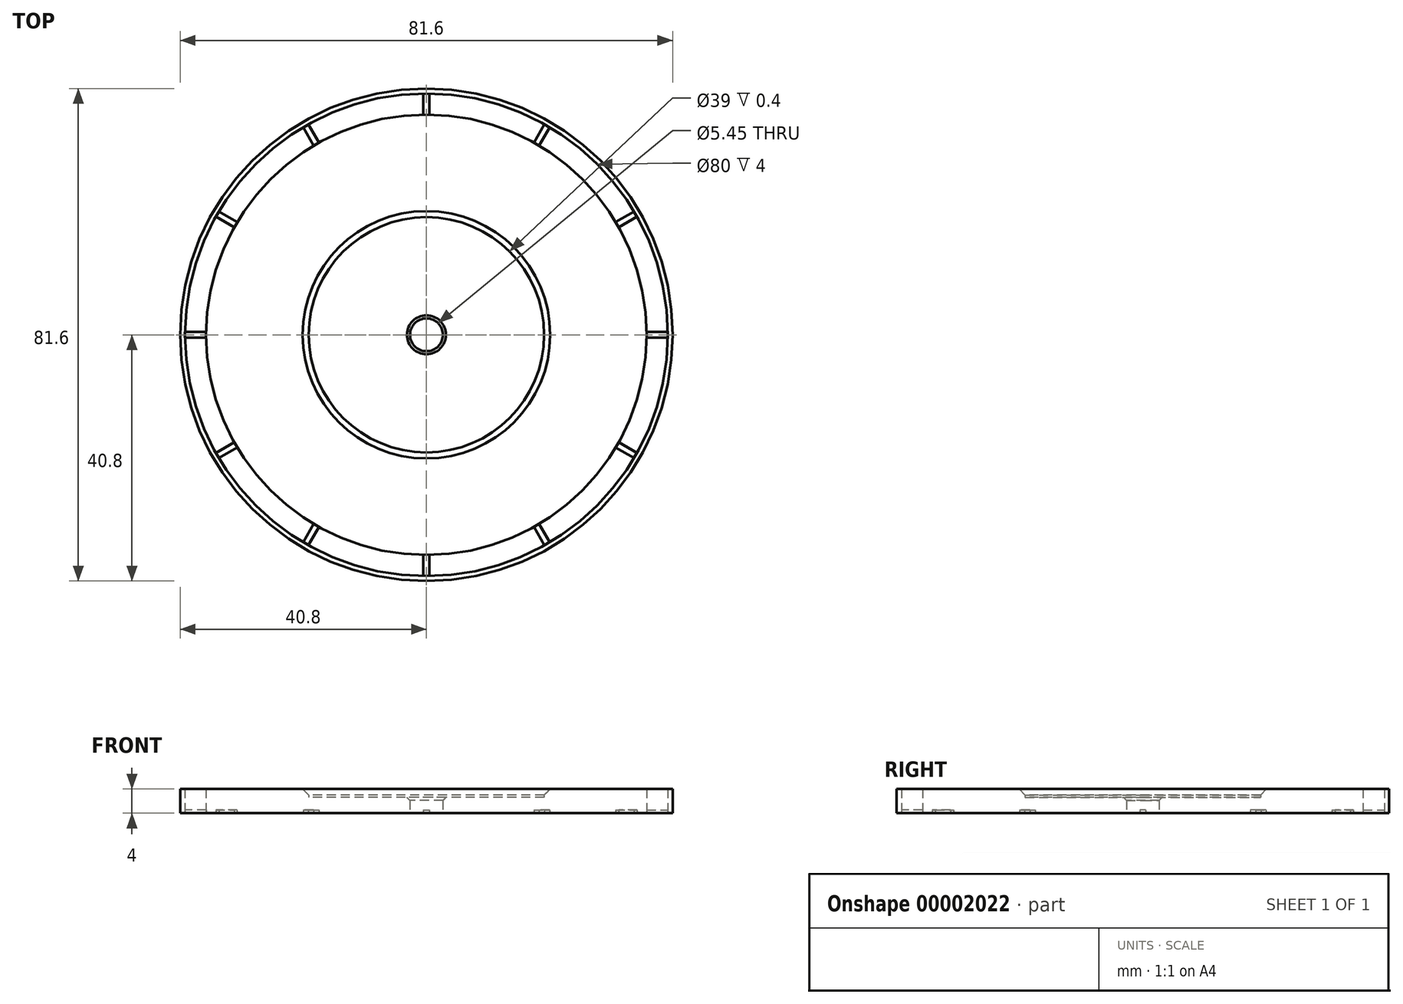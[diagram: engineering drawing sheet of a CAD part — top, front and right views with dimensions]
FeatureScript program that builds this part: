
annotation { "Feature Type Name" : "Feature", "Feature Type Description" : "" }
export const myFeature = defineFeature(function(context is Context, id is Id, definition is map)
    precondition{}
    {
        {
            var Q0;
            Q0=qCreatedBy(makeId("Top.planeOp"),FACE);
            var sketch = newSketch(context, id + "F0", { "sketchPlane" : qUnion([Q0])});
            skCircle(sketch, "E0", {"center": v(0, 0) * mm, "radius": 36.5 * mm});
            skCircle(sketch, "E1", {"center": v(0, 0) * mm, "radius": 40 * mm});
            skCircle(sketch, "E2", {"center": v(0, 0) * mm, "radius": 40.8 * mm});
            skCircle(sketch, "E3", {"center": v(0, 0) * mm, "radius": 19.5 * mm});
            skCircle(sketch, "E4", {"center": v(0, 0) * mm, "radius": 2.73 * mm});
            skSolve(sketch);
        }
        {
            var Q0;
            Q0=makeQuery(id+"F0.imprint","IMPRINT",FACE,{"disambiguationData":[TD([[makeQuery(id+"F0.imprint","IMPRINT",EDGE,{"derivedFrom":sQuery(id+"F0.wireOp",EDGE,"E0")}),1.0]])]});
            var Q1;
            Q1=makeQuery(id+"F0.imprint","IMPRINT",FACE,{"disambiguationData":[TD([[makeQuery(id+"F0.imprint","IMPRINT",EDGE,{"derivedFrom":sQuery(id+"F0.wireOp",EDGE,"E1")}),-1.0]])]});
            extrude(context, id + "F1", {"entities" : qUnion([Q0, Q1]), "depth" : 4 * mm});
        }
        {
            var Q0;
            Q0=makeQuery(id+"F0.imprint","IMPRINT",FACE,{"disambiguationData":[TD([[makeQuery(id+"F0.imprint","IMPRINT",EDGE,{"derivedFrom":sQuery(id+"F0.wireOp",EDGE,"E3")}),1.0]])]});
            extrude(context, id + "F2", {"entities" : qUnion([Q0]), "operationType" : NewBodyOperationType.ADD, "depth" : (8 - 5.4) * mm});
        }
        {
            var Q0;
            {var subQ0=sQuery(id+"F0.wireOp",EDGE,"E3");Q0=makeQuery(id+"F2.boolean.opBoolean","MERGE",FACE,{"derivedFrom":[makeQuery(id+"F1.opExtrude","CAP_FACE",FACE,{"disambiguationData":[OSD([sQuery(id+"F0.wireOp",EDGE,"E0"),subQ0])],"isStart":true}),makeQuery(id+"F2.opExtrude","CAP_FACE",FACE,{"disambiguationData":[OSD([subQ0,sQuery(id+"F0.wireOp",EDGE,"E4")])],"isStart":true})]});}
            var sketch = newSketch(context, id + "F3", { "sketchPlane" : qUnion([Q0])});
            skLineSegment(sketch, "E5", {"start": v(0, 0) * mm, "end": v(0, 38.64) * mm, "construction": true});
            skLineSegment(sketch, "E6", {"start": v(-0.5, 36.5) * mm, "end": v(-0.5, 40) * mm});
            skLineSegment(sketch, "E7", {"start": v(-0.5, 40) * mm, "end": v(0.5, 40) * mm});
            skLineSegment(sketch, "E8", {"start": v(0.5, 40) * mm, "end": v(0.5, 36.5) * mm});
            skPoint(sketch, "E9", {"position": v(0, 40) * mm});
            skCircle(sketch, "E10.0", {"center": v(0, 0) * mm, "radius": 40 * mm, "construction": true});
            skSolve(sketch);
        }
        {
            var Q0;
            {var subQ2=sQuery(id+"F3.wireOp",EDGE,"E6");Q0=makeQuery(id+"F3.imprint","IMPRINT",FACE,{"disambiguationData":[TD([[makeQuery(id+"F3.imprint","IMPRINT",EDGE,{"derivedFrom":subQ2}),-1.0]])]});}
            var Q1;
            Q1=makeQuery(id+"F1.opExtrude","CAP_FACE",FACE,{"disambiguationData":[OSD([sQuery(id+"F0.wireOp",EDGE,"E0"),sQuery(id+"F0.wireOp",EDGE,"E3")])],"isStart":false});
            extrude(context, id + "F4", {"entities" : qUnion([Q0]), "oppositeDirection" : true, "endBoundEntity" : qUnion([Q1]), "depth" : .5 * mm});
        }
        {
            var Q0;
            Q0=makeQuery(id+"F4.opExtrude","SWEPT_BODY",BODY,{"disambiguationData":[OSD([sQuery(id+"F0.wireOp",EDGE,"E0"),sQuery(id+"F3.wireOp",EDGE,"E6"),sQuery(id+"F3.wireOp",EDGE,"E7"),sQuery(id+"F3.wireOp",EDGE,"E8")])]});
            var Q1;
            Q1=makeQuery(id+"F1.opExtrude","SWEPT_FACE",FACE,{"disambiguationData":[OSD([sQuery(id+"F0.wireOp",EDGE,"E3")])]});
            circularPattern(context, id + "F5", {"entities" : qUnion([Q0]), "axis" : qUnion([Q1]), "angle" : 360 * degree, "instanceCount" : round(12), "equalSpace" : true});
        }
        {
            var Q0;
            Q0=makeQuery(id+"F1.opExtrude","CAP_EDGE",EDGE,{"disambiguationData":[OSD([sQuery(id+"F0.wireOp",EDGE,"E3")])],"isStart":false});
            chamfer(context, id + "F6", {"entities" : qUnion([Q0]), "width" : 1 * mm, "tangentPropagation" : true});
        }
        {
            var Q0;
            Q0=makeQuery(id+"F2.opExtrude","CAP_EDGE",EDGE,{"disambiguationData":[OSD([sQuery(id+"F0.wireOp",EDGE,"E4")])],"isStart":false});
            chamfer(context, id + "F7", {"entities" : qUnion([Q0]), "width" : .5 * mm, "tangentPropagation" : true});
        }
    });
